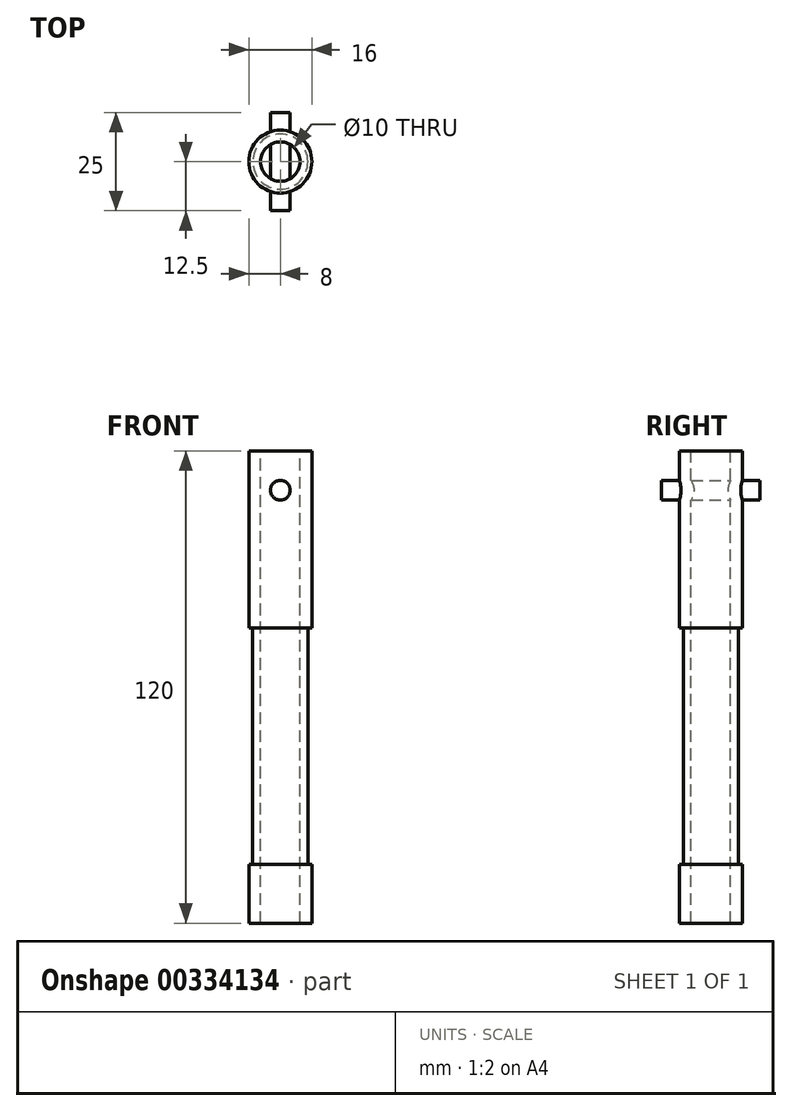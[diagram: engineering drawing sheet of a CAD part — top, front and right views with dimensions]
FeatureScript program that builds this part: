
annotation { "Feature Type Name" : "Feature", "Feature Type Description" : "" }
export const myFeature = defineFeature(function(context is Context, id is Id, definition is map)
    precondition{}
    {
        {
            var Q0;
            Q0=qCreatedBy(makeId("Front.planeOp"),FACE);
            var sketch = newSketch(context, id + "F0", { "sketchPlane" : qUnion([Q0])});
            skLineSegment(sketch, "E0", {"start": v(5, 51) * mm, "end": v(8, 51) * mm});
            skLineSegment(sketch, "E1", {"start": v(8, 51) * mm, "end": v(8, 6) * mm});
            skLineSegment(sketch, "E2", {"start": v(8, 6) * mm, "end": v(7, 6) * mm});
            skLineSegment(sketch, "E3", {"start": v(7, 6) * mm, "end": v(7, -54) * mm});
            skLineSegment(sketch, "E4", {"start": v(7, -54) * mm, "end": v(8, -54) * mm});
            skLineSegment(sketch, "E5", {"start": v(8, -54) * mm, "end": v(8, -69) * mm});
            skLineSegment(sketch, "E6", {"start": v(8, -69) * mm, "end": v(5, -69) * mm});
            skLineSegment(sketch, "E7", {"start": v(5, -69) * mm, "end": v(5, 51) * mm});
            skLineSegment(sketch, "E8", {"start": v(0, 36.07) * mm, "end": v(0, -81.1) * mm, "construction": true});
            skSolve(sketch);
        }
        {
            var Q0;
            Q0 = qSketchRegion(id + "F0", true);
            var Q1;
            Q1=sQuery(id+"F0.wireOp",EDGE,"E8");
            revolve(context, id + "F1", {"entities" : qUnion([Q0]), "axis" : qUnion([Q1]), "revolveType" : RevolveType.FULL});
        }
        {
            var Q0;
            Q0=qCreatedBy(makeId("Front.planeOp"),FACE);
            var sketch = newSketch(context, id + "F2", { "sketchPlane" : qUnion([Q0])});
            skCircle(sketch, "E9", {"center": v(0, 41) * mm, "radius": 2.5 * mm});
            skSolve(sketch);
        }
        {
            var Q0;
            Q0 = qSketchRegion(id + "F2", true);
            extrude(context, id + "F3", {"entities" : qUnion([Q0]), "operationType" : NewBodyOperationType.ADD, "depth" : 25 * mm, "symmetric" : true});
        }
    });
